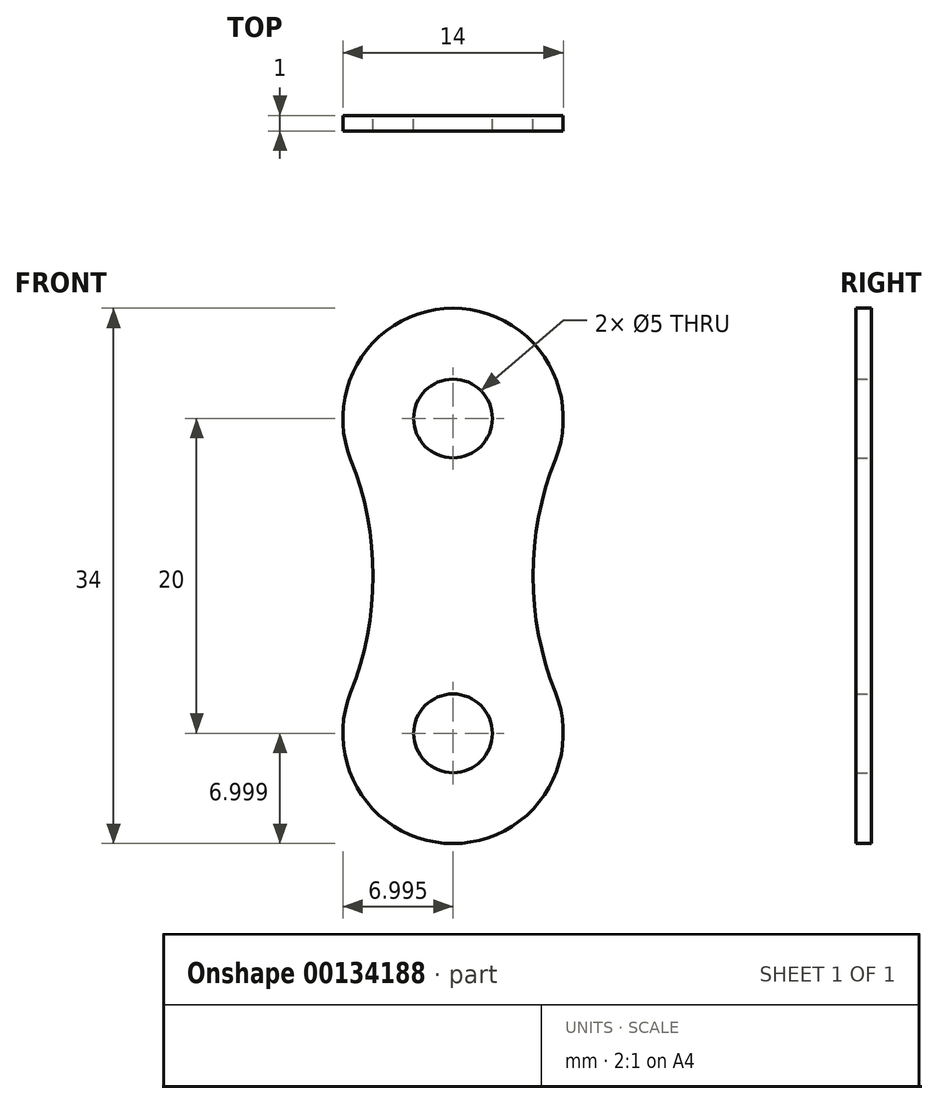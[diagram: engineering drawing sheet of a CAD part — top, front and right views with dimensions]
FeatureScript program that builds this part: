
annotation { "Feature Type Name" : "Feature", "Feature Type Description" : "" }
export const myFeature = defineFeature(function(context is Context, id is Id, definition is map)
    precondition{}
    {
        {
            var Q0;
            Q0=qCreatedBy(makeId("Front.planeOp"),FACE);
            var sketch = newSketch(context, id + "F0", { "sketchPlane" : qUnion([Q0])});
            skArc(sketch, "E0", {"start": v(-3.95, 16.58) * mm, "mid": v(-10.45, 26.17) * mm, "end": v(-16.96, 16.58) * mm});
            skArc(sketch, "E1", {"start": v(-16.96, 1.76) * mm, "mid": v(-10.45, -7.83) * mm, "end": v(-3.95, 1.76) * mm});
            skArc(sketch, "E2", {"start": v(-16.96, 1.76) * mm, "mid": v(-15.53, 9.17) * mm, "end": v(-16.96, 16.58) * mm});
            skArc(sketch, "E3", {"start": v(-3.95, 16.58) * mm, "mid": v(-5.37, 9.17) * mm, "end": v(-3.95, 1.76) * mm});
            skCircle(sketch, "E4", {"center": v(-10.45, 19.17) * mm, "radius": 2.5 * mm});
            skCircle(sketch, "E5", {"center": v(-10.45, -0.83) * mm, "radius": 2.5 * mm});
            skSolve(sketch);
        }
        {
            var Q0;
            Q0=makeQuery(id+"F0.imprint","IMPRINT",FACE,{"disambiguationData":[TD([[makeQuery(id+"F0.imprint","IMPRINT",EDGE,{"derivedFrom":sQuery(id+"F0.wireOp",EDGE,"E0")}),1.0]])]});
            extrude(context, id + "F1", {"entities" : qUnion([Q0]), "depth" : 1 * mm});
        }
    });
